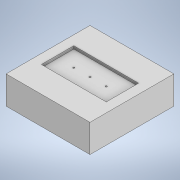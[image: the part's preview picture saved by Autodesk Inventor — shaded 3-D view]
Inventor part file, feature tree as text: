
AUTODESK INVENTOR PART (.ipt)
format: ipt  version: 2022 (Build 260153000, 153)  size: 122,368 bytes
history: native  units: mm
features: extrude x4, sketch x4
ambient origin geometry x8: Origin, YZ Plane, XZ Plane, XY Plane, X Axis, Y Axis, Z Axis, Center Point
bodies: Solid1 (feature_tree)
feature tree (8):
  extrude  "Extrusion1"  Depth=150.0mm
  extrude  "Extrusion2"  Depth=5.0mm TaperAngle=0.0deg
  extrude  "Extrusion3"  Depth=5.0mm TaperAngle=0.0deg
  extrude  "Extrusion4"  Depth=25.0mm TaperAngle=0.0deg
  sketch  "Sketch1"  dims[d0=150.0mm d1=150.0mm]
  sketch  "Sketch2"  dims[d2=50.0mm d3=0.0mm d9=5.0mm d10=0.0mm]
  sketch  "Sketch3"  dims[d14=3.0mm d15=5.0mm d16=0.0mm]
  sketch  "Sketch4"  dims[d17=8.0mm d18=25.0mm d19=0.0mm]
